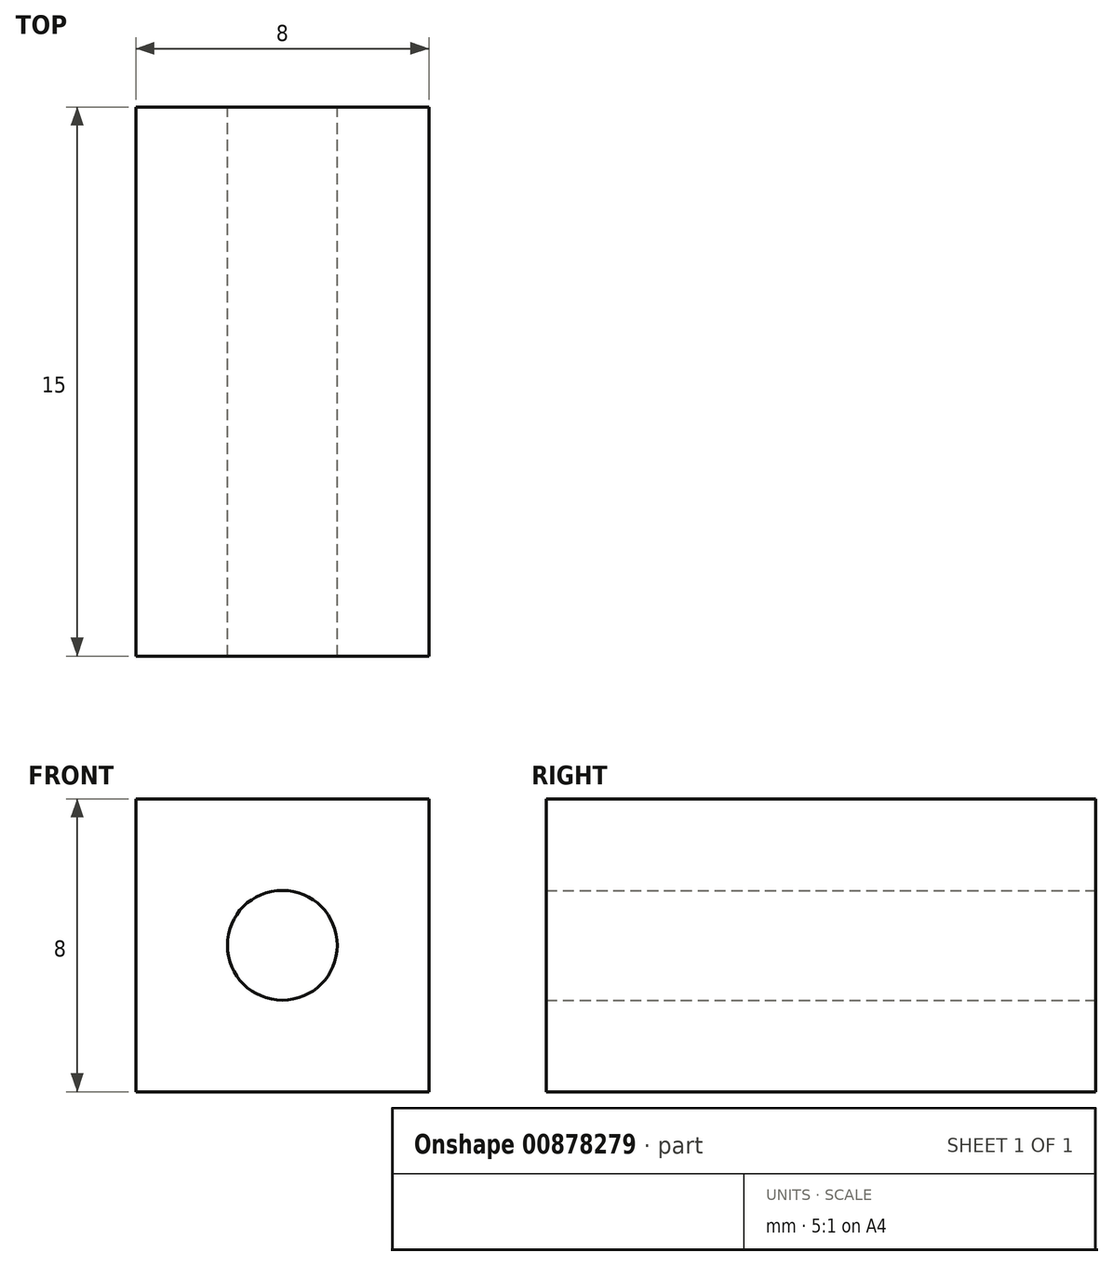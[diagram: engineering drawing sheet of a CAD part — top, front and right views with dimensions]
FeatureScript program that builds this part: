
annotation { "Feature Type Name" : "Feature", "Feature Type Description" : "" }
export const myFeature = defineFeature(function(context is Context, id is Id, definition is map)
    precondition{}
    {
        {
            var Q0;
            Q0=qCreatedBy(makeId("Front.planeOp"),FACE);
            var sketch = newSketch(context, id + "F0", { "sketchPlane" : qUnion([Q0])});
            skLineSegment(sketch, "E0.bottom", {"start": v(4, -4) * mm, "end": v(-4, -4) * mm});
            skLineSegment(sketch, "E0.top", {"start": v(4, 4) * mm, "end": v(-4, 4) * mm});
            skLineSegment(sketch, "E0.left", {"start": v(4, -4) * mm, "end": v(4, 4) * mm});
            skLineSegment(sketch, "E0.right", {"start": v(-4, -4) * mm, "end": v(-4, 4) * mm});
            skPoint(sketch, "E0.middle", {"position": v(0, 0) * mm});
            skCircle(sketch, "E1", {"center": v(0, 0) * mm, "radius": 1.5 * mm});
            skSolve(sketch);
        }
        {
            var Q0;
            Q0=makeQuery(id+"F0.imprint","IMPRINT",FACE,{"disambiguationData":[TD([[makeQuery(id+"F0.imprint","IMPRINT",EDGE,{"derivedFrom":sQuery(id+"F0.wireOp",EDGE,"E0.bottom")}),-1.0]])]});
            extrude(context, id + "F1", {"entities" : qUnion([Q0]), "depth" : 15 * mm, "offsetDistance" : 25 * mm});
        }
    });
